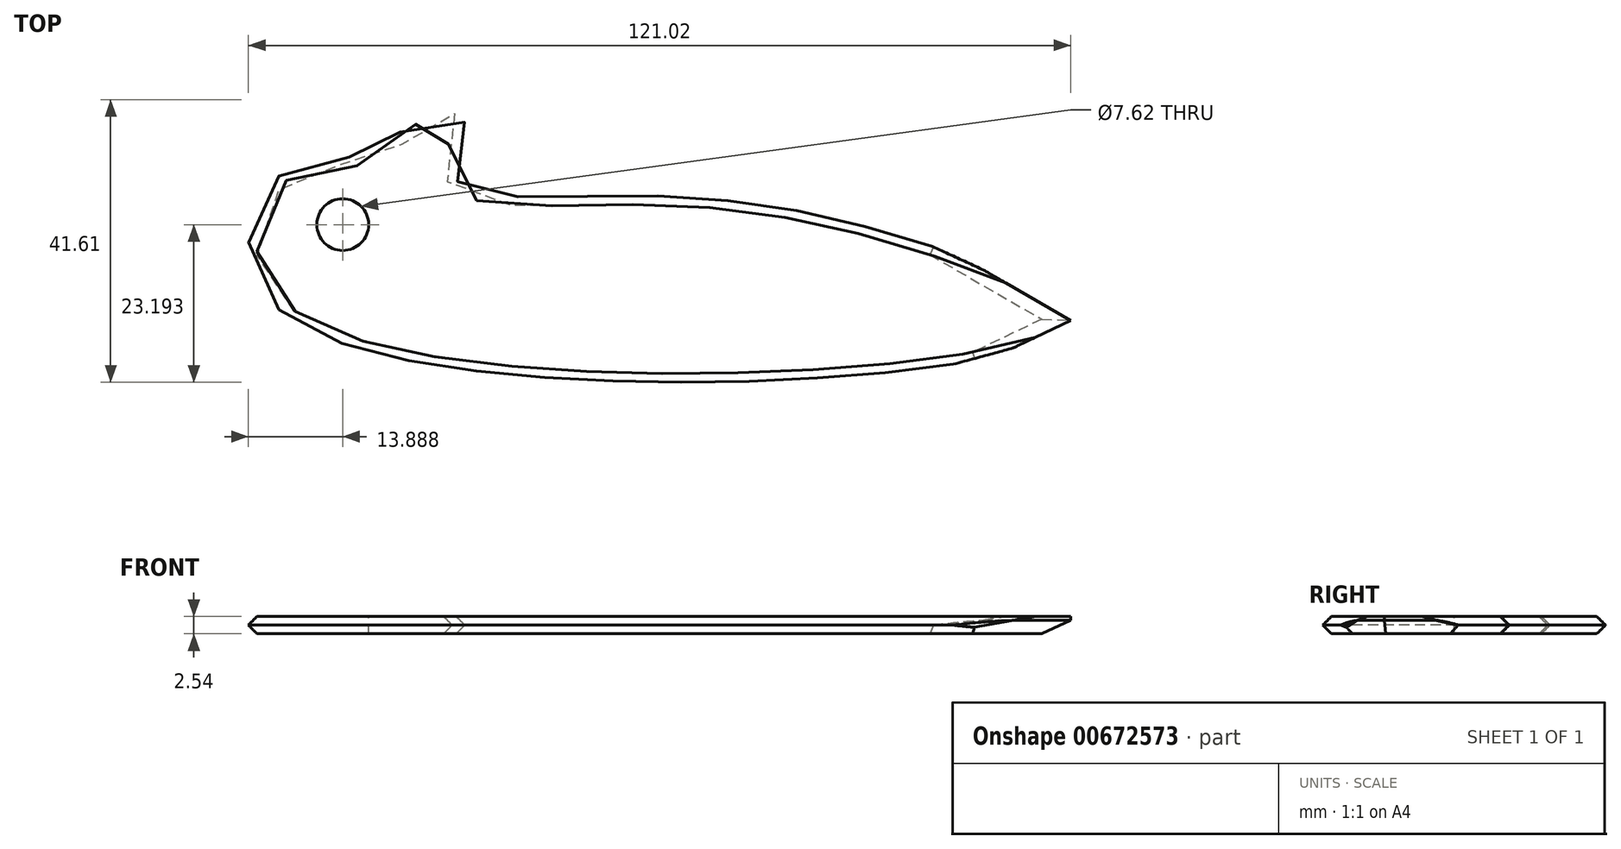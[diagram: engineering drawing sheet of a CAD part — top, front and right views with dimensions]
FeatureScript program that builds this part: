
annotation { "Feature Type Name" : "Feature", "Feature Type Description" : "" }
export const myFeature = defineFeature(function(context is Context, id is Id, definition is map)
    precondition{}
    {
        {
            var Q0;
            Q0=qCreatedBy(makeId("Top.planeOp"),FACE);
            var sketch = newSketch(context, id + "F0", { "sketchPlane" : qUnion([Q0])});
            skFitSpline(sketch, "E0", {"points": [v(-1.27, 27.92) * mm, v(-8.04, 20.54) * mm, v(-17.96, 20.13) * mm, v(-25.14, 14.17) * mm, v(-27.72, 3.84) * mm, v(-15.3, -8.3) * mm, v(68.64, -13.07) * mm, v(95.07, -4.54) * mm, v(68.2, 8.46) * mm, v(28.9, 14.24) * mm, v(3.77, 16.84) * mm, v(5.36, 25.8) * mm, v(-1.27, 27.92) * mm]});
            skSolve(sketch);
        }
        {
            var Q0;
            Q0=makeQuery(id+"F0.imprint","IMPRINT",FACE,{"disambiguationData":[TD([[makeQuery(id+"F0.imprint","IMPRINT",EDGE,{"derivedFrom":sQuery(id+"F0.wireOp",EDGE,"E0")}),1.0]])]});
            extrude(context, id + "F1", {"entities" : qUnion([Q0]), "depth" : 2.54 * mm, "offsetDistance" : 25.4 * mm});
        }
        {
            var Q0;
            Q0=makeQuery(id+"F1.opExtrude","CAP_FACE",FACE,{"disambiguationData":[OSD([sQuery(id+"F0.wireOp",EDGE,"E0")])],"isStart":false});
            var sketch = newSketch(context, id + "F2", { "sketchPlane" : qUnion([Q0])});
            skLineSegment(sketch, "E1", {"start": v(68.49, 8.37) * mm, "end": v(81.1, 2.56) * mm});
            skLineSegment(sketch, "E2", {"start": v(81.1, 2.56) * mm, "end": v(93.9, -4.85) * mm});
            skLineSegment(sketch, "E3", {"start": v(93.9, -4.85) * mm, "end": v(85.43, -8.9) * mm});
            skLineSegment(sketch, "E4", {"start": v(85.43, -8.9) * mm, "end": v(71.26, -12.77) * mm});
            skSolve(sketch);
        }
        {
            var Q0;
            {var subQ1=sQuery(id+"F2.wireOp",EDGE,"E1");Q0=makeQuery(id+"F2.imprint","IMPRINT",FACE,{"disambiguationData":[TD([[makeQuery(id+"F2.imprint","IMPRINT",EDGE,{"derivedFrom":subQ1}),1.0]])]});}
            extrude(context, id + "F3", {"entities" : qUnion([Q0]), "operationType" : NewBodyOperationType.REMOVE, "endBound" : BoundingType.THROUGH_ALL, "oppositeDirection" : true, "depth" : 25.4 * mm, "offsetDistance" : 25.4 * mm});
        }
        {
            var Q0;
            Q0=makeQuery(id+"F1.opExtrude","CAP_FACE",FACE,{"disambiguationData":[OSD([sQuery(id+"F0.wireOp",EDGE,"E0")])],"isStart":false});
            var sketch = newSketch(context, id + "F4", { "sketchPlane" : qUnion([Q0])});
            skCircle(sketch, "E5", {"center": v(-13.23, 9.25) * mm, "radius": 3.81 * mm});
            skSolve(sketch);
        }
        {
            var Q0;
            Q0=makeQuery(id+"F4.imprint","IMPRINT",FACE,{"disambiguationData":[TD([[makeQuery(id+"F4.imprint","IMPRINT",EDGE,{"derivedFrom":sQuery(id+"F4.wireOp",EDGE,"E5")}),1.0]])]});
            extrude(context, id + "F5", {"entities" : qUnion([Q0]), "operationType" : NewBodyOperationType.REMOVE, "endBound" : BoundingType.THROUGH_ALL, "oppositeDirection" : true, "depth" : 25.4 * mm, "offsetDistance" : 25.4 * mm});
        }
        {
            var Q0;
            Q0=makeQuery(id+"F1.opExtrude","CAP_EDGE",EDGE,{"disambiguationData":[OSD([sQuery(id+"F0.wireOp",EDGE,"E0")])],"isStart":true});
            var Q1;
            Q1=makeQuery(id+"F3.boolean.opBoolean","COPY",EDGE,{"derivedFrom":makeQuery(id+"F3.opExtrude","CAP_EDGE",EDGE,{"disambiguationData":[OSD([sQuery(id+"F2.wireOp",EDGE,"E1")])],"isStart":true})});
            var Q2;
            Q2=makeQuery(id+"F3.boolean.opBoolean","COPY",EDGE,{"derivedFrom":makeQuery(id+"F3.opExtrude","CAP_EDGE",EDGE,{"disambiguationData":[OSD([sQuery(id+"F2.wireOp",EDGE,"E2")])],"isStart":true})});
            var Q3;
            Q3=makeQuery(id+"F3.boolean.opBoolean","COPY",EDGE,{"derivedFrom":makeQuery(id+"F3.opExtrude","CAP_EDGE",EDGE,{"disambiguationData":[OSD([sQuery(id+"F2.wireOp",EDGE,"E3")])],"isStart":true})});
            var Q4;
            Q4=makeQuery(id+"F3.boolean.opBoolean","COPY",EDGE,{"derivedFrom":makeQuery(id+"F3.opExtrude","CAP_EDGE",EDGE,{"disambiguationData":[OSD([sQuery(id+"F2.wireOp",EDGE,"E4")])],"isStart":true})});
            var Q5;
            Q5=makeQuery(id+"F1.opExtrude","CAP_EDGE",EDGE,{"disambiguationData":[OSD([sQuery(id+"F0.wireOp",EDGE,"E0")])],"isStart":false});
            chamfer(context, id + "F6", {"entities" : qUnion([Q0, Q1, Q2, Q3, Q4, Q5]), "width" : 2 * mm, "tangentPropagation" : true});
        }
        {
            var Q0;
            Q0=makeQuery(id+"F3.boolean.opBoolean","INTERSECT",EDGE,{"derivedFrom":[makeQuery(id+"F1.opExtrude","CAP_FACE",FACE,{"disambiguationData":[OSD([sQuery(id+"F0.wireOp",EDGE,"E0")])],"isStart":true}),makeQuery(id+"F3.opExtrude","SWEPT_FACE",FACE,{"disambiguationData":[OSD([sQuery(id+"F2.wireOp",EDGE,"E2")])]})]});
            var Q1;
            Q1=makeQuery(id+"F3.boolean.opBoolean","INTERSECT",EDGE,{"derivedFrom":[makeQuery(id+"F1.opExtrude","CAP_FACE",FACE,{"disambiguationData":[OSD([sQuery(id+"F0.wireOp",EDGE,"E0")])],"isStart":true}),makeQuery(id+"F3.opExtrude","SWEPT_FACE",FACE,{"disambiguationData":[OSD([sQuery(id+"F2.wireOp",EDGE,"E3")])]})]});
            chamfer(context, id + "F7", {"entities" : qUnion([Q0, Q1]), "width" : 2 * mm, "tangentPropagation" : true});
        }
    });
